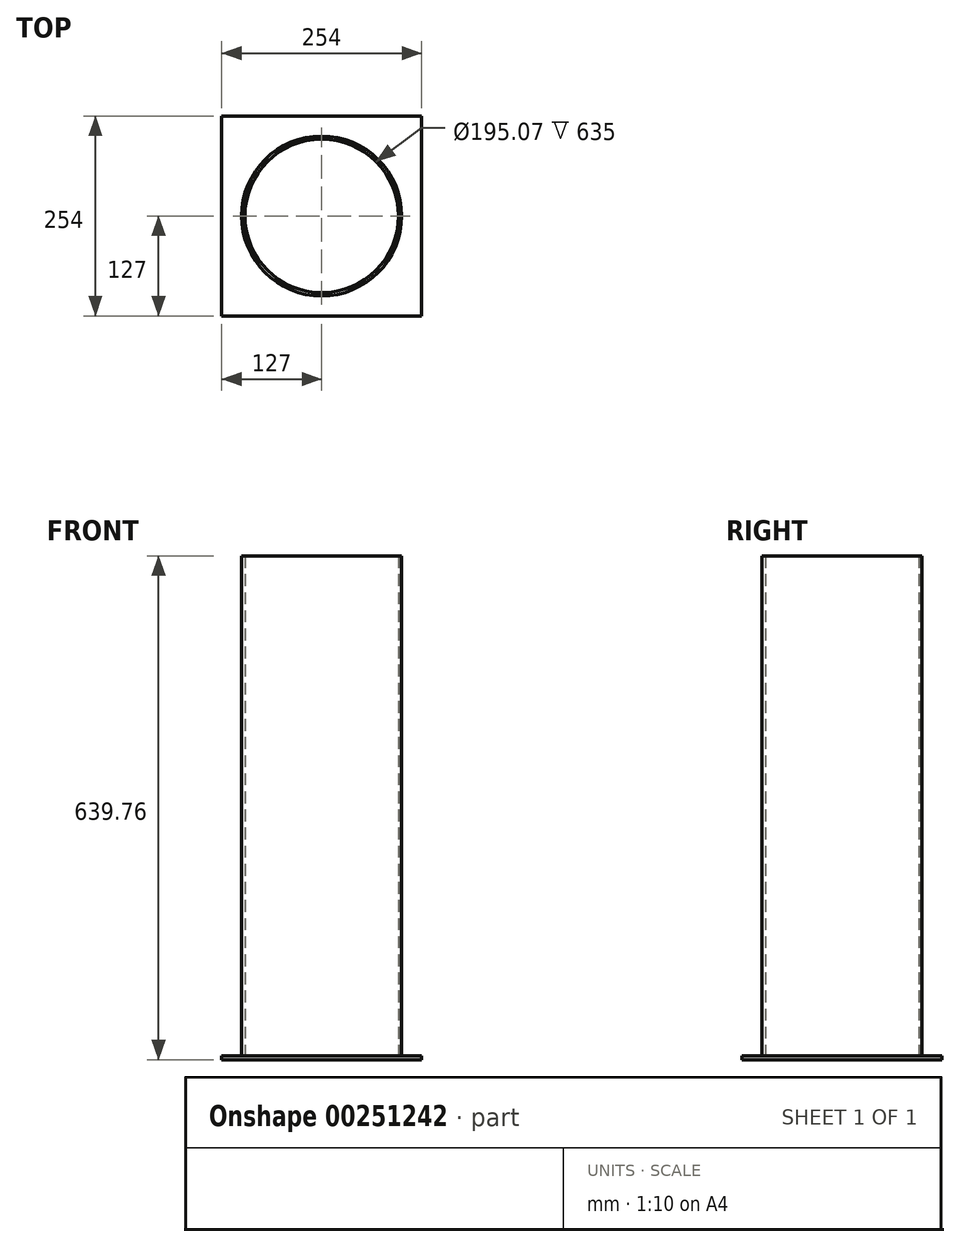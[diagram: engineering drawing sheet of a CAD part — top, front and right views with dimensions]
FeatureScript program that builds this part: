
annotation { "Feature Type Name" : "Feature", "Feature Type Description" : "" }
export const myFeature = defineFeature(function(context is Context, id is Id, definition is map)
    precondition{}
    {
        {
            var Q0;
            Q0=qCreatedBy(makeId("Top.planeOp"),FACE);
            var sketch = newSketch(context, id + "F0", { "sketchPlane" : qUnion([Q0])});
            skCircle(sketch, "E0", {"center": v(0, 0) * mm, "radius": 101.6 * mm});
            skCircle(sketch, "E1.0", {"center": v(0, 0) * mm, "radius": 97.54 * mm});
            skSolve(sketch);
        }
        {
            var Q0;
            Q0 = qSketchRegion(id + "F0", true);
            extrude(context, id + "F1", {"entities" : qUnion([Q0]), "depth" : 635 * mm});
        }
        {
            var Q0;
            Q0=qCreatedBy(makeId("Top.planeOp"),FACE);
            var sketch = newSketch(context, id + "F2", { "sketchPlane" : qUnion([Q0])});
            skLineSegment(sketch, "E2.bottom", {"start": v(127, 127) * mm, "end": v(-127, 127) * mm});
            skLineSegment(sketch, "E2.top", {"start": v(127, -127) * mm, "end": v(-127, -127) * mm});
            skLineSegment(sketch, "E2.left", {"start": v(127, 127) * mm, "end": v(127, -127) * mm});
            skLineSegment(sketch, "E2.right", {"start": v(-127, 127) * mm, "end": v(-127, -127) * mm});
            skPoint(sketch, "E2.middle", {"position": v(0, 0) * mm});
            skSolve(sketch);
        }
        {
            var Q0;
            Q0 = qSketchRegion(id + "F2", true);
            extrude(context, id + "F3", {"entities" : qUnion([Q0]), "operationType" : NewBodyOperationType.ADD, "oppositeDirection" : true, "depth" : 4.76 * mm});
        }
    });
